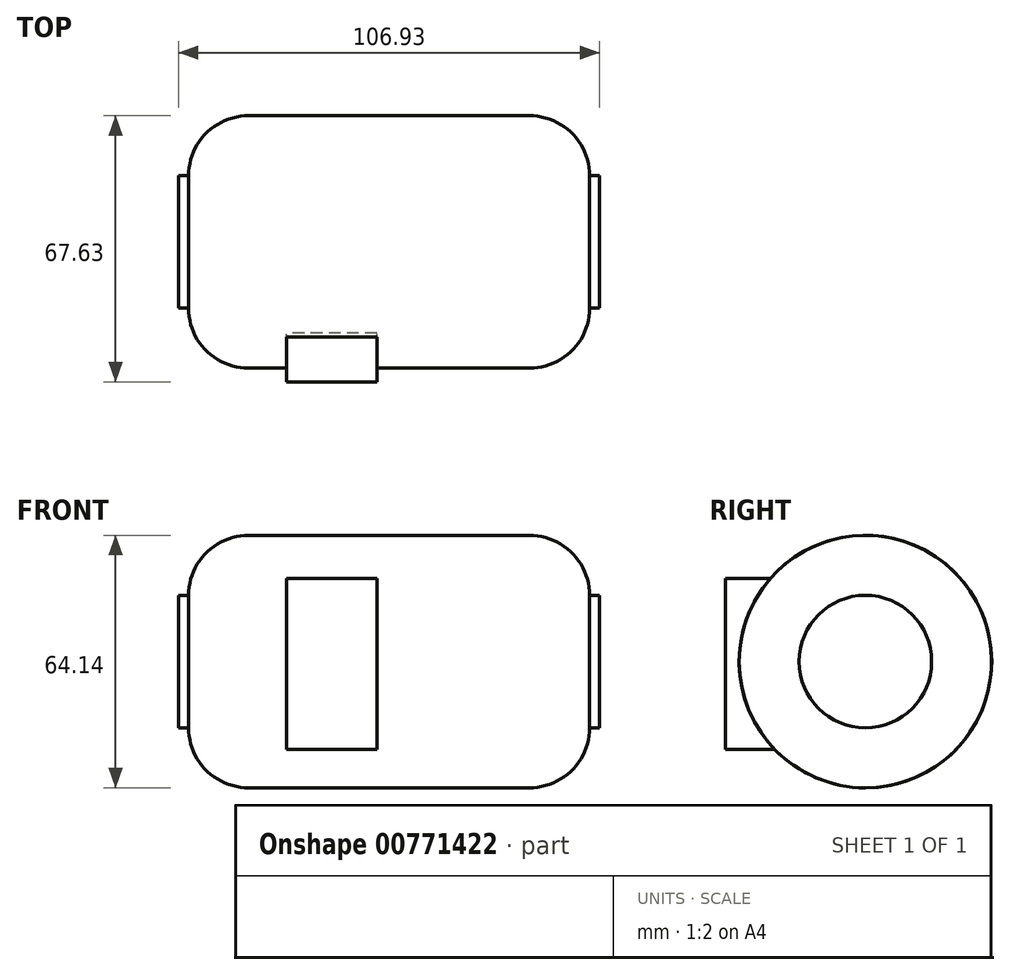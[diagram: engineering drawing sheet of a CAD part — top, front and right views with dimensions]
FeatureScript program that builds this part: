
annotation { "Feature Type Name" : "Feature", "Feature Type Description" : "" }
export const myFeature = defineFeature(function(context is Context, id is Id, definition is map)
    precondition{}
    {
        {
            var Q0;
            Q0=qCreatedBy(makeId("Right.planeOp"),FACE);
            var sketch = newSketch(context, id + "F0", { "sketchPlane" : qUnion([Q0])});
            skCircle(sketch, "E0", {"center": v(0, 0) * mm, "radius": 32.07 * mm});
            skSolve(sketch);
        }
        {
            var Q0;
            Q0=makeQuery(id+"F0.imprint","IMPRINT",FACE,{"disambiguationData":[TD([[makeQuery(id+"F0.imprint","IMPRINT",EDGE,{"derivedFrom":sQuery(id+"F0.wireOp",EDGE,"E0")}),1.0]])]});
            extrude(context, id + "F1", {"entities" : qUnion([Q0]), "depth" : 101.85 * mm, "offsetDistance" : 25.4 * mm});
        }
        {
            var Q0;
            Q0=makeQuery(id+"F1.opExtrude","CAP_FACE",FACE,{"disambiguationData":[OSD([sQuery(id+"F0.wireOp",EDGE,"E0")])],"isStart":false});
            var Q1;
            Q1=makeQuery(id+"F1.opExtrude","SWEPT_FACE",FACE,{"disambiguationData":[OSD([sQuery(id+"F0.wireOp",EDGE,"E0")])]});
            fillet(context, id + "F2", {"entities" : qUnion([Q0, Q1]), "radius" : 15.24 * mm, "tangentPropagation" : true, "allowEdgeOverflow" : false});
        }
        {
            var Q0;
            Q0=makeQuery(id+"F1.opExtrude","CAP_FACE",FACE,{"disambiguationData":[OSD([sQuery(id+"F0.wireOp",EDGE,"E0")])],"isStart":false});
            extrude(context, id + "F3", {"entities" : qUnion([Q0]), "operationType" : NewBodyOperationType.ADD, "depth" : 2.54 * mm, "offsetDistance" : 25.4 * mm});
        }
        {
            var Q0;
            Q0=makeQuery(id+"F1.opExtrude","CAP_FACE",FACE,{"disambiguationData":[OSD([sQuery(id+"F0.wireOp",EDGE,"E0")])],"isStart":true});
            extrude(context, id + "F4", {"entities" : qUnion([Q0]), "operationType" : NewBodyOperationType.ADD, "depth" : 2.54 * mm, "offsetDistance" : 25.4 * mm});
        }
        {
            var Q0;
            Q0=qCreatedBy(makeId("Front.planeOp"),FACE);
            var sketch = newSketch(context, id + "F5", { "sketchPlane" : qUnion([Q0])});
            skLineSegment(sketch, "E1.bottom", {"start": v(24.88, 21.16) * mm, "end": v(47.82, 21.16) * mm});
            skLineSegment(sketch, "E1.top", {"start": v(24.88, -22.26) * mm, "end": v(47.82, -22.26) * mm});
            skLineSegment(sketch, "E1.left", {"start": v(24.88, 21.16) * mm, "end": v(24.88, -22.26) * mm});
            skLineSegment(sketch, "E1.right", {"start": v(47.82, 21.16) * mm, "end": v(47.82, -22.26) * mm});
            skSolve(sketch);
        }
        {
            var Q0;
            Q0 = qSketchRegion(id + "F5", true);
            extrude(context, id + "F6", {"entities" : qUnion([Q0]), "operationType" : NewBodyOperationType.ADD, "depth" : 35.56 * mm, "offsetDistance" : 25.4 * mm});
        }
        {
            var Q0;
            Q0=makeQuery(id+"F3.opExtrude","CAP_FACE",FACE,{"disambiguationData":[OSD([sQuery(id+"F0.wireOp",EDGE,"E0")])],"isStart":false});
            extrude(context, id + "F7", {"entities" : qUnion([Q0]), "operationType" : NewBodyOperationType.ADD, "oppositeDirection" : true, "depth" : 25.4 * mm, "offsetDistance" : 25.4 * mm});
        }
    });
